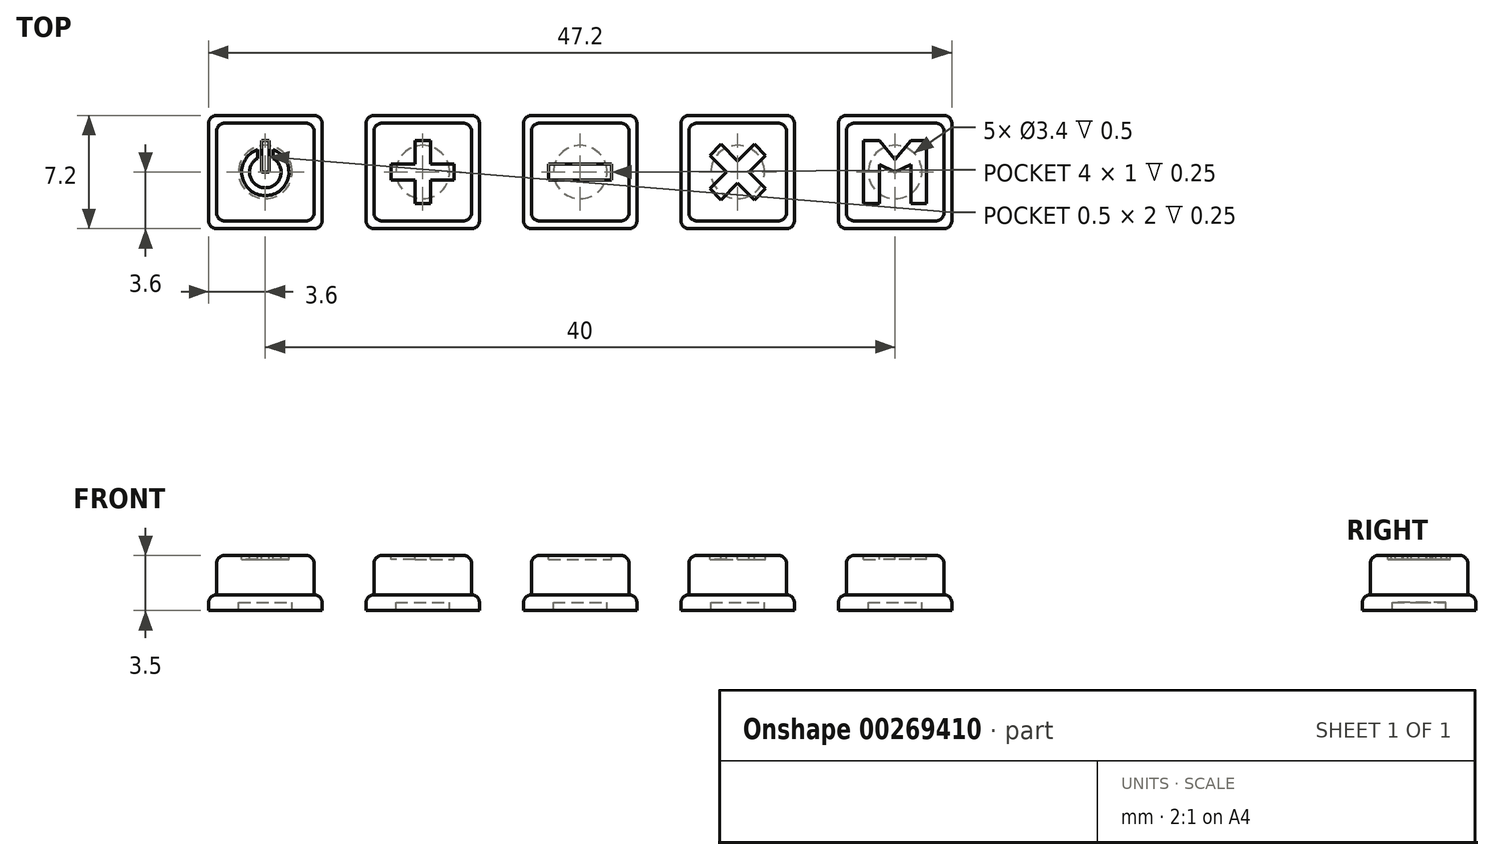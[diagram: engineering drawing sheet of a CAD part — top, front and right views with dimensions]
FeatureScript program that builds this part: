
annotation { "Feature Type Name" : "Feature", "Feature Type Description" : "" }
export const myFeature = defineFeature(function(context is Context, id is Id, definition is map)
    precondition{}
    {
        {
            var Q0;
            Q0=qCreatedBy(makeId("Top.planeOp"),FACE);
            var sketch = newSketch(context, id + "F0", { "sketchPlane" : qUnion([Q0])});
            skLineSegment(sketch, "E0.bottom", {"start": v(2.6, 3.1) * mm, "end": v(-2.6, 3.1) * mm});
            skLineSegment(sketch, "E0.top", {"start": v(2.6, -3.1) * mm, "end": v(-2.6, -3.1) * mm});
            skLineSegment(sketch, "E0.left", {"start": v(3.1, 2.6) * mm, "end": v(3.1, -2.6) * mm});
            skLineSegment(sketch, "E0.right", {"start": v(-3.1, 2.6) * mm, "end": v(-3.1, -2.6) * mm});
            skPoint(sketch, "E0.middle", {"position": v(0, 0) * mm});
            skPoint(sketch, "E1.visualSharp", {"position": v(-3.1, 3.1) * mm});
            skArc(sketch, "E1.filletArc", {"start": v(-2.6, 3.1) * mm, "mid": v(-2.95, 2.95) * mm, "end": v(-3.1, 2.6) * mm});
            skPoint(sketch, "E2.visualSharp", {"position": v(-3.1, -3.1) * mm});
            skArc(sketch, "E2.filletArc", {"start": v(-3.1, -2.6) * mm, "mid": v(-2.95, -2.95) * mm, "end": v(-2.6, -3.1) * mm});
            skPoint(sketch, "E3.visualSharp", {"position": v(3.1, -3.1) * mm});
            skArc(sketch, "E3.filletArc", {"start": v(2.6, -3.1) * mm, "mid": v(2.95, -2.95) * mm, "end": v(3.1, -2.6) * mm});
            skPoint(sketch, "E4.visualSharp", {"position": v(3.1, 3.1) * mm});
            skArc(sketch, "E4.filletArc", {"start": v(3.1, 2.6) * mm, "mid": v(2.95, 2.95) * mm, "end": v(2.6, 3.1) * mm});
            skSolve(sketch);
        }
        {
            var Q0;
            Q0=makeQuery(id+"F0.imprint","IMPRINT",FACE,{"disambiguationData":[TD([[makeQuery(id+"F0.imprint","IMPRINT",EDGE,{"derivedFrom":sQuery(id+"F0.wireOp",EDGE,"E0.bottom")}),1.0]])]});
            extrude(context, id + "F1", {"entities" : qUnion([Q0]), "depth" : 2.5 * mm});
        }
        {
            var Q0;
            Q0=makeQuery(id+"F1.opExtrude","CAP_FACE",FACE,{"disambiguationData":[OSD([sQuery(id+"F0.wireOp",EDGE,"E0.bottom"),sQuery(id+"F0.wireOp",EDGE,"E0.top"),sQuery(id+"F0.wireOp",EDGE,"E0.left"),sQuery(id+"F0.wireOp",EDGE,"E0.right"),sQuery(id+"F0.wireOp",EDGE,"E1.filletArc"),sQuery(id+"F0.wireOp",EDGE,"E2.filletArc"),sQuery(id+"F0.wireOp",EDGE,"E3.filletArc"),sQuery(id+"F0.wireOp",EDGE,"E4.filletArc")])],"isStart":true});
            var sketch = newSketch(context, id + "F2", { "sketchPlane" : qUnion([Q0])});
            skLineSegment(sketch, "E5.bottom", {"start": v(3.1, 3.6) * mm, "end": v(-3.1, 3.6) * mm});
            skLineSegment(sketch, "E5.top", {"start": v(3.1, -3.6) * mm, "end": v(-3.1, -3.6) * mm});
            skLineSegment(sketch, "E5.left", {"start": v(3.6, 3.1) * mm, "end": v(3.6, -3.1) * mm});
            skLineSegment(sketch, "E5.right", {"start": v(-3.6, 3.1) * mm, "end": v(-3.6, -3.1) * mm});
            skPoint(sketch, "E5.middle", {"position": v(0, 0) * mm});
            skPoint(sketch, "E6.visualSharp", {"position": v(3.6, 3.6) * mm});
            skArc(sketch, "E6.filletArc", {"start": v(3.6, 3.1) * mm, "mid": v(3.45, 3.45) * mm, "end": v(3.1, 3.6) * mm});
            skPoint(sketch, "E7.visualSharp", {"position": v(3.6, -3.6) * mm});
            skArc(sketch, "E7.filletArc", {"start": v(3.1, -3.6) * mm, "mid": v(3.45, -3.45) * mm, "end": v(3.6, -3.1) * mm});
            skPoint(sketch, "E8.visualSharp", {"position": v(-3.6, -3.6) * mm});
            skArc(sketch, "E8.filletArc", {"start": v(-3.6, -3.1) * mm, "mid": v(-3.45, -3.45) * mm, "end": v(-3.1, -3.6) * mm});
            skPoint(sketch, "E9.visualSharp", {"position": v(-3.6, 3.6) * mm});
            skArc(sketch, "E9.filletArc", {"start": v(-3.1, 3.6) * mm, "mid": v(-3.45, 3.45) * mm, "end": v(-3.6, 3.1) * mm});
            skCircle(sketch, "E10", {"center": v(0, 0) * mm, "radius": 1.7 * mm});
            skSolve(sketch);
        }
        {
            var Q0;
            Q0 = qSketchRegion(id + "F2", true);
            extrude(context, id + "F3", {"entities" : qUnion([Q0]), "operationType" : NewBodyOperationType.ADD, "depth" : 1 * mm});
        }
        {
            var Q0;
            Q0=makeQuery(id+"F1.opExtrude","CAP_FACE",FACE,{"disambiguationData":[OSD([sQuery(id+"F0.wireOp",EDGE,"E0.bottom"),sQuery(id+"F0.wireOp",EDGE,"E0.top"),sQuery(id+"F0.wireOp",EDGE,"E0.left"),sQuery(id+"F0.wireOp",EDGE,"E0.right"),sQuery(id+"F0.wireOp",EDGE,"E1.filletArc"),sQuery(id+"F0.wireOp",EDGE,"E2.filletArc"),sQuery(id+"F0.wireOp",EDGE,"E3.filletArc"),sQuery(id+"F0.wireOp",EDGE,"E4.filletArc")])],"isStart":true});
            extrude(context, id + "F4", {"entities" : qUnion([Q0]), "operationType" : NewBodyOperationType.ADD, "depth" : 0.5 * mm});
        }
        {
            var Q0;
            Q0=makeQuery(id+"F1.opExtrude","CAP_FACE",FACE,{"disambiguationData":[OSD([sQuery(id+"F0.wireOp",EDGE,"E0.bottom"),sQuery(id+"F0.wireOp",EDGE,"E0.top"),sQuery(id+"F0.wireOp",EDGE,"E0.left"),sQuery(id+"F0.wireOp",EDGE,"E0.right"),sQuery(id+"F0.wireOp",EDGE,"E1.filletArc"),sQuery(id+"F0.wireOp",EDGE,"E2.filletArc"),sQuery(id+"F0.wireOp",EDGE,"E3.filletArc"),sQuery(id+"F0.wireOp",EDGE,"E4.filletArc")])],"isStart":false});
            var Q1;
            Q1=makeQuery(id+"F3.opExtrude","CAP_EDGE",EDGE,{"disambiguationData":[OSD([sQuery(id+"F2.wireOp",EDGE,"E5.right")])],"isStart":true});
            fillet(context, id + "F5", {"entities" : qUnion([Q0, Q1]), "radius" : 0.5 * mm, "tangentPropagation" : true, "allowEdgeOverflow" : false});
        }
        {
            var Q0;
            Q0=makeQuery(id+"F1.opExtrude","SWEPT_BODY",BODY,{"disambiguationData":[OSD([sQuery(id+"F0.wireOp",EDGE,"E0.bottom"),sQuery(id+"F0.wireOp",EDGE,"E0.top"),sQuery(id+"F0.wireOp",EDGE,"E0.left"),sQuery(id+"F0.wireOp",EDGE,"E0.right"),sQuery(id+"F0.wireOp",EDGE,"E1.filletArc"),sQuery(id+"F0.wireOp",EDGE,"E2.filletArc"),sQuery(id+"F0.wireOp",EDGE,"E3.filletArc"),sQuery(id+"F0.wireOp",EDGE,"E4.filletArc")])]});
            transform(context, id + "F6", {"entities" : qUnion([Q0]), "transformType" : TransformType.TRANSLATION_3D, "dx" : 10 * mm, "dy" : 0 * mm, "dz" : 0 * mm, "makeCopy" : true});
        }
        {
            var Q0;
            Q0=makeQuery(id+"F6.opPattern","COPY",BODY,{"derivedFrom":makeQuery(id+"F1.opExtrude","SWEPT_BODY",BODY,{"disambiguationData":[OSD([sQuery(id+"F0.wireOp",EDGE,"E0.bottom"),sQuery(id+"F0.wireOp",EDGE,"E0.top"),sQuery(id+"F0.wireOp",EDGE,"E0.left"),sQuery(id+"F0.wireOp",EDGE,"E0.right"),sQuery(id+"F0.wireOp",EDGE,"E1.filletArc"),sQuery(id+"F0.wireOp",EDGE,"E2.filletArc"),sQuery(id+"F0.wireOp",EDGE,"E3.filletArc"),sQuery(id+"F0.wireOp",EDGE,"E4.filletArc")])]}),"instanceName":"1"});
            transform(context, id + "F7", {"entities" : qUnion([Q0]), "transformType" : TransformType.TRANSLATION_3D, "dx" : 10 * mm, "dy" : 0 * mm, "dz" : 0 * mm, "makeCopy" : true});
        }
        {
            var Q0;
            Q0=makeQuery(id+"F7.opPattern","COPY",BODY,{"derivedFrom":makeQuery(id+"F6.opPattern","COPY",BODY,{"derivedFrom":makeQuery(id+"F1.opExtrude","SWEPT_BODY",BODY,{"disambiguationData":[OSD([sQuery(id+"F0.wireOp",EDGE,"E0.bottom"),sQuery(id+"F0.wireOp",EDGE,"E0.top"),sQuery(id+"F0.wireOp",EDGE,"E0.left"),sQuery(id+"F0.wireOp",EDGE,"E0.right"),sQuery(id+"F0.wireOp",EDGE,"E1.filletArc"),sQuery(id+"F0.wireOp",EDGE,"E2.filletArc"),sQuery(id+"F0.wireOp",EDGE,"E3.filletArc"),sQuery(id+"F0.wireOp",EDGE,"E4.filletArc")])]}),"instanceName":"1"}),"instanceName":"1"});
            transform(context, id + "F8", {"entities" : qUnion([Q0]), "transformType" : TransformType.TRANSLATION_3D, "dx" : 10 * mm, "dy" : 0 * mm, "dz" : 0 * mm, "makeCopy" : true});
        }
        {
            var Q0;
            Q0=makeQuery(id+"F8.opPattern","COPY",BODY,{"derivedFrom":makeQuery(id+"F7.opPattern","COPY",BODY,{"derivedFrom":makeQuery(id+"F6.opPattern","COPY",BODY,{"derivedFrom":makeQuery(id+"F1.opExtrude","SWEPT_BODY",BODY,{"disambiguationData":[OSD([sQuery(id+"F0.wireOp",EDGE,"E0.bottom"),sQuery(id+"F0.wireOp",EDGE,"E0.top"),sQuery(id+"F0.wireOp",EDGE,"E0.left"),sQuery(id+"F0.wireOp",EDGE,"E0.right"),sQuery(id+"F0.wireOp",EDGE,"E1.filletArc"),sQuery(id+"F0.wireOp",EDGE,"E2.filletArc"),sQuery(id+"F0.wireOp",EDGE,"E3.filletArc"),sQuery(id+"F0.wireOp",EDGE,"E4.filletArc")])]}),"instanceName":"1"}),"instanceName":"1"}),"instanceName":"1"});
            transform(context, id + "F9", {"entities" : qUnion([Q0]), "transformType" : TransformType.TRANSLATION_3D, "dx" : 10 * mm, "dy" : 0 * mm, "dz" : 0 * mm, "makeCopy" : true});
        }
        {
            var Q0;
            Q0=makeQuery(id+"F1.opExtrude","CAP_FACE",FACE,{"disambiguationData":[OSD([sQuery(id+"F0.wireOp",EDGE,"E0.bottom"),sQuery(id+"F0.wireOp",EDGE,"E0.top"),sQuery(id+"F0.wireOp",EDGE,"E0.left"),sQuery(id+"F0.wireOp",EDGE,"E0.right"),sQuery(id+"F0.wireOp",EDGE,"E1.filletArc"),sQuery(id+"F0.wireOp",EDGE,"E2.filletArc"),sQuery(id+"F0.wireOp",EDGE,"E3.filletArc"),sQuery(id+"F0.wireOp",EDGE,"E4.filletArc")])],"isStart":false});
            var sketch = newSketch(context, id + "F10", { "sketchPlane" : qUnion([Q0])});
            skArc(sketch, "E11", {"start": v(-0.5, 0.87) * mm, "mid": v(0, -1) * mm, "end": v(0.5, 0.87) * mm});
            skArc(sketch, "E12", {"start": v(-0.5, 1.41) * mm, "mid": v(0, -1.5) * mm, "end": v(0.5, 1.41) * mm});
            skLineSegment(sketch, "E13", {"start": v(0.25, 2) * mm, "end": v(0.25, 0) * mm});
            skLineSegment(sketch, "E14", {"start": v(0.25, 0) * mm, "end": v(-0.25, 0) * mm});
            skLineSegment(sketch, "E15", {"start": v(-0.25, 0) * mm, "end": v(-0.25, 2) * mm});
            skLineSegment(sketch, "E16", {"start": v(-0.25, 2) * mm, "end": v(0.25, 2) * mm});
            skLineSegment(sketch, "E17.0", {"start": v(0.5, 1.41) * mm, "end": v(0.5, 0.87) * mm});
            skLineSegment(sketch, "E18", {"start": v(0, 2) * mm, "end": v(0, 0) * mm, "construction": true});
            skLineSegment(sketch, "E19.0", {"start": v(-0.5, 0.87) * mm, "end": v(-0.5, 1.41) * mm});
            skSolve(sketch);
        }
        {
            var Q0;
            Q0=makeQuery(id+"F6.opPattern","COPY",FACE,{"derivedFrom":makeQuery(id+"F1.opExtrude","CAP_FACE",FACE,{"disambiguationData":[OSD([sQuery(id+"F0.wireOp",EDGE,"E0.bottom"),sQuery(id+"F0.wireOp",EDGE,"E0.top"),sQuery(id+"F0.wireOp",EDGE,"E0.left"),sQuery(id+"F0.wireOp",EDGE,"E0.right"),sQuery(id+"F0.wireOp",EDGE,"E1.filletArc"),sQuery(id+"F0.wireOp",EDGE,"E2.filletArc"),sQuery(id+"F0.wireOp",EDGE,"E3.filletArc"),sQuery(id+"F0.wireOp",EDGE,"E4.filletArc")])],"isStart":false}),"instanceName":"1"});
            var sketch = newSketch(context, id + "F11", { "sketchPlane" : qUnion([Q0])});
            skLineSegment(sketch, "E20", {"start": v(12.6, 0) * mm, "end": v(7.4, 0) * mm, "construction": true});
            skLineSegment(sketch, "E21", {"start": v(10, 2.6) * mm, "end": v(10, -2.6) * mm, "construction": true});
            skLineSegment(sketch, "E22", {"start": v(10, 2) * mm, "end": v(10.5, 2) * mm});
            skLineSegment(sketch, "E23", {"start": v(10.5, 2) * mm, "end": v(10.5, 0.5) * mm});
            skLineSegment(sketch, "E24", {"start": v(10.5, 0.5) * mm, "end": v(12, 0.5) * mm});
            skLineSegment(sketch, "E25", {"start": v(12, 0.5) * mm, "end": v(12, 0) * mm});
            skLineSegment(sketch, "E26", {"start": v(12, 0) * mm, "end": v(12, -0.5) * mm});
            skLineSegment(sketch, "E27", {"start": v(12, -0.5) * mm, "end": v(10.5, -0.5) * mm});
            skLineSegment(sketch, "E28", {"start": v(10.5, -0.5) * mm, "end": v(10.5, -2) * mm});
            skLineSegment(sketch, "E29", {"start": v(10.5, -2) * mm, "end": v(10, -2) * mm});
            skLineSegment(sketch, "E30.MirrorCS", {"start": v(10, 2) * mm, "end": v(9.5, 2) * mm});
            skLineSegment(sketch, "E31.MirrorCS", {"start": v(9.5, 2) * mm, "end": v(9.5, 0.5) * mm});
            skLineSegment(sketch, "E32.MirrorCS", {"start": v(9.5, 0.5) * mm, "end": v(8, 0.5) * mm});
            skLineSegment(sketch, "E33.MirrorCS", {"start": v(8, 0.5) * mm, "end": v(8, 0) * mm});
            skLineSegment(sketch, "E34.MirrorCS", {"start": v(8, -0.5) * mm, "end": v(9.5, -0.5) * mm});
            skLineSegment(sketch, "E35.MirrorCS", {"start": v(9.5, -0.5) * mm, "end": v(9.5, -2) * mm});
            skLineSegment(sketch, "E36.MirrorCS", {"start": v(9.5, -2) * mm, "end": v(10, -2) * mm});
            skLineSegment(sketch, "E37.MirrorCS", {"start": v(8, 0) * mm, "end": v(8, -0.5) * mm});
            skSolve(sketch);
        }
        {
            var Q0;
            Q0=makeQuery(id+"F7.opPattern","COPY",FACE,{"derivedFrom":makeQuery(id+"F6.opPattern","COPY",FACE,{"derivedFrom":makeQuery(id+"F1.opExtrude","CAP_FACE",FACE,{"disambiguationData":[OSD([sQuery(id+"F0.wireOp",EDGE,"E0.bottom"),sQuery(id+"F0.wireOp",EDGE,"E0.top"),sQuery(id+"F0.wireOp",EDGE,"E0.left"),sQuery(id+"F0.wireOp",EDGE,"E0.right"),sQuery(id+"F0.wireOp",EDGE,"E1.filletArc"),sQuery(id+"F0.wireOp",EDGE,"E2.filletArc"),sQuery(id+"F0.wireOp",EDGE,"E3.filletArc"),sQuery(id+"F0.wireOp",EDGE,"E4.filletArc")])],"isStart":false}),"instanceName":"1"}),"instanceName":"1"});
            var sketch = newSketch(context, id + "F12", { "sketchPlane" : qUnion([Q0])});
            skLineSegment(sketch, "E38", {"start": v(17.4, 0) * mm, "end": v(22.6, 0) * mm, "construction": true});
            skLineSegment(sketch, "E39", {"start": v(20, 2.6) * mm, "end": v(20, -2.6) * mm, "construction": true});
            skLineSegment(sketch, "E40", {"start": v(18, 0.5) * mm, "end": v(22, 0.5) * mm});
            skLineSegment(sketch, "E41", {"start": v(22, 0.5) * mm, "end": v(22, -0.5) * mm});
            skLineSegment(sketch, "E42", {"start": v(22, -0.5) * mm, "end": v(18, -0.5) * mm});
            skLineSegment(sketch, "E43", {"start": v(18, -0.5) * mm, "end": v(18, 0.5) * mm});
            skSolve(sketch);
        }
        {
            var Q0;
            Q0=makeQuery(id+"F8.opPattern","COPY",FACE,{"derivedFrom":makeQuery(id+"F7.opPattern","COPY",FACE,{"derivedFrom":makeQuery(id+"F6.opPattern","COPY",FACE,{"derivedFrom":makeQuery(id+"F1.opExtrude","CAP_FACE",FACE,{"disambiguationData":[OSD([sQuery(id+"F0.wireOp",EDGE,"E0.bottom"),sQuery(id+"F0.wireOp",EDGE,"E0.top"),sQuery(id+"F0.wireOp",EDGE,"E0.left"),sQuery(id+"F0.wireOp",EDGE,"E0.right"),sQuery(id+"F0.wireOp",EDGE,"E1.filletArc"),sQuery(id+"F0.wireOp",EDGE,"E2.filletArc"),sQuery(id+"F0.wireOp",EDGE,"E3.filletArc"),sQuery(id+"F0.wireOp",EDGE,"E4.filletArc")])],"isStart":false}),"instanceName":"1"}),"instanceName":"1"}),"instanceName":"1"});
            var sketch = newSketch(context, id + "F13", { "sketchPlane" : qUnion([Q0])});
            skLineSegment(sketch, "E44", {"start": v(30, 2.6) * mm, "end": v(30, -2.6) * mm, "construction": true});
            skLineSegment(sketch, "E45", {"start": v(27.4, 0) * mm, "end": v(32.6, 0) * mm, "construction": true});
            skLineSegment(sketch, "E46", {"start": v(31.06, 1.77) * mm, "end": v(31.77, 1.06) * mm});
            skLineSegment(sketch, "E47", {"start": v(31.77, 1.06) * mm, "end": v(30.7, 0) * mm});
            skLineSegment(sketch, "E48", {"start": v(30.7, 0) * mm, "end": v(31.77, -1.06) * mm});
            skLineSegment(sketch, "E49", {"start": v(31.77, -1.06) * mm, "end": v(31.06, -1.77) * mm});
            skLineSegment(sketch, "E50", {"start": v(31.06, -1.77) * mm, "end": v(30, -0.7) * mm});
            skLineSegment(sketch, "E51", {"start": v(30, -0.7) * mm, "end": v(28.94, -1.77) * mm});
            skLineSegment(sketch, "E52", {"start": v(28.94, -1.77) * mm, "end": v(28.23, -1.06) * mm});
            skLineSegment(sketch, "E53", {"start": v(28.23, -1.06) * mm, "end": v(29.3, 0) * mm});
            skLineSegment(sketch, "E54", {"start": v(29.3, 0) * mm, "end": v(28.23, 1.06) * mm});
            skLineSegment(sketch, "E55", {"start": v(28.23, 1.06) * mm, "end": v(28.94, 1.77) * mm});
            skLineSegment(sketch, "E56", {"start": v(28.94, 1.77) * mm, "end": v(30, 0.7) * mm});
            skLineSegment(sketch, "E57", {"start": v(30, 0.7) * mm, "end": v(31.06, 1.77) * mm});
            skSolve(sketch);
        }
        {
            var Q0;
            Q0=makeQuery(id+"F9.opPattern","COPY",FACE,{"derivedFrom":makeQuery(id+"F8.opPattern","COPY",FACE,{"derivedFrom":makeQuery(id+"F7.opPattern","COPY",FACE,{"derivedFrom":makeQuery(id+"F6.opPattern","COPY",FACE,{"derivedFrom":makeQuery(id+"F1.opExtrude","CAP_FACE",FACE,{"disambiguationData":[OSD([sQuery(id+"F0.wireOp",EDGE,"E0.bottom"),sQuery(id+"F0.wireOp",EDGE,"E0.top"),sQuery(id+"F0.wireOp",EDGE,"E0.left"),sQuery(id+"F0.wireOp",EDGE,"E0.right"),sQuery(id+"F0.wireOp",EDGE,"E1.filletArc"),sQuery(id+"F0.wireOp",EDGE,"E2.filletArc"),sQuery(id+"F0.wireOp",EDGE,"E3.filletArc"),sQuery(id+"F0.wireOp",EDGE,"E4.filletArc")])],"isStart":false}),"instanceName":"1"}),"instanceName":"1"}),"instanceName":"1"}),"instanceName":"1"});
            var sketch = newSketch(context, id + "F14", { "sketchPlane" : qUnion([Q0])});
            skLineSegment(sketch, "E58", {"start": v(40, 2.6) * mm, "end": v(40, -2.6) * mm, "construction": true});
            skLineSegment(sketch, "E59", {"start": v(37.4, 0) * mm, "end": v(42.6, 0) * mm, "construction": true});
            skLineSegment(sketch, "E60", {"start": v(38, 2) * mm, "end": v(39, 2) * mm});
            skLineSegment(sketch, "E61", {"start": v(39, 2) * mm, "end": v(40, 0.8) * mm});
            skLineSegment(sketch, "E62", {"start": v(40, 0.8) * mm, "end": v(41, 2) * mm});
            skLineSegment(sketch, "E63", {"start": v(41, 2) * mm, "end": v(42, 2) * mm});
            skLineSegment(sketch, "E64", {"start": v(42, 2) * mm, "end": v(42, -2) * mm});
            skLineSegment(sketch, "E65", {"start": v(42, -2) * mm, "end": v(41, -2) * mm});
            skLineSegment(sketch, "E66", {"start": v(41, -2) * mm, "end": v(41, 0.47) * mm});
            skLineSegment(sketch, "E67", {"start": v(41, 0.47) * mm, "end": v(40, 0) * mm});
            skLineSegment(sketch, "E68", {"start": v(40, 0) * mm, "end": v(39, 0.47) * mm});
            skLineSegment(sketch, "E69", {"start": v(39, 0.47) * mm, "end": v(39, -2) * mm});
            skLineSegment(sketch, "E70", {"start": v(39, -2) * mm, "end": v(38, -2) * mm});
            skLineSegment(sketch, "E71", {"start": v(38, -2) * mm, "end": v(38, 2) * mm});
            skSolve(sketch);
        }
        {
            var Q0;
            Q0=makeQuery(id+"F10.imprint","IMPRINT",FACE,{"disambiguationData":[TD([[makeQuery(id+"F10.imprint","IMPRINT",EDGE,{"derivedFrom":sQuery(id+"F10.wireOp",EDGE,"E11")}),-1.0]])]});
            var Q1;
            Q1=makeQuery(id+"F10.imprint","IMPRINT",FACE,{"disambiguationData":[TD([[makeQuery(id+"F10.imprint","IMPRINT",EDGE,{"derivedFrom":sQuery(id+"F10.wireOp",EDGE,"E13")}),-1.0]])]});
            extrude(context, id + "F15", {"entities" : qUnion([Q0, Q1]), "operationType" : NewBodyOperationType.REMOVE, "oppositeDirection" : true, "depth" : 0.25 * mm});
        }
        {
            var Q0;
            Q0=makeQuery(id+"F11.imprint","IMPRINT",FACE,{"disambiguationData":[TD([[makeQuery(id+"F11.imprint","IMPRINT",EDGE,{"derivedFrom":sQuery(id+"F11.wireOp",EDGE,"E22")}),-1.0]])]});
            extrude(context, id + "F16", {"entities" : qUnion([Q0]), "operationType" : NewBodyOperationType.REMOVE, "oppositeDirection" : true, "depth" : 0.25 * mm});
        }
        {
            var Q0;
            Q0=makeQuery(id+"F12.imprint","IMPRINT",FACE,{"disambiguationData":[TD([[makeQuery(id+"F12.imprint","IMPRINT",EDGE,{"derivedFrom":sQuery(id+"F12.wireOp",EDGE,"E40")}),-1.0]])]});
            extrude(context, id + "F17", {"entities" : qUnion([Q0]), "operationType" : NewBodyOperationType.REMOVE, "oppositeDirection" : true, "depth" : 0.25 * mm});
        }
        {
            var Q0;
            Q0=makeQuery(id+"F13.imprint","IMPRINT",FACE,{"disambiguationData":[TD([[makeQuery(id+"F13.imprint","IMPRINT",EDGE,{"derivedFrom":sQuery(id+"F13.wireOp",EDGE,"E46")}),-1.0]])]});
            extrude(context, id + "F18", {"entities" : qUnion([Q0]), "operationType" : NewBodyOperationType.REMOVE, "oppositeDirection" : true, "depth" : 0.25 * mm});
        }
        {
            var Q0;
            Q0=makeQuery(id+"F14.imprint","IMPRINT",FACE,{"disambiguationData":[TD([[makeQuery(id+"F14.imprint","IMPRINT",EDGE,{"derivedFrom":sQuery(id+"F14.wireOp",EDGE,"E60")}),-1.0]])]});
            extrude(context, id + "F19", {"entities" : qUnion([Q0]), "operationType" : NewBodyOperationType.REMOVE, "oppositeDirection" : true, "depth" : 0.25 * mm});
        }
    });
